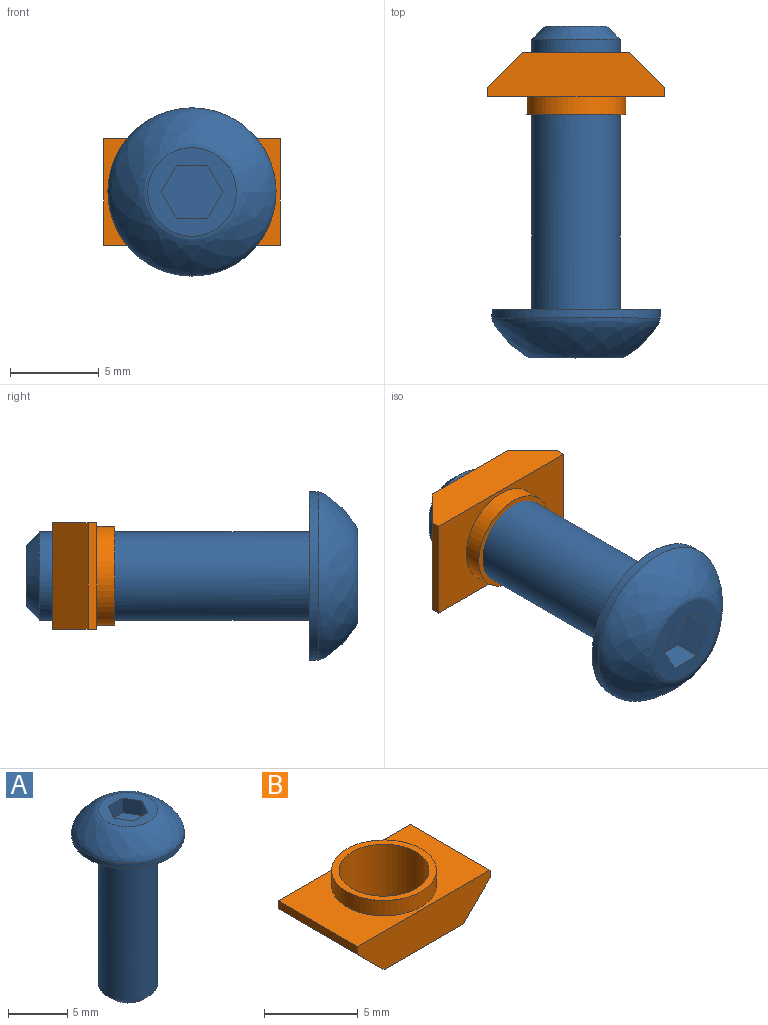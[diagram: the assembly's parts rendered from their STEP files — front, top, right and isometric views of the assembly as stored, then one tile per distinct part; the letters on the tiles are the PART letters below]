
ASSEMBLY  parts=2 mates=1
PART A: 14 faces, bbox 9.5x9.5x18.8 mm
  f0: plane 5.01x5.01mm, normal (0,0,1), area 11.8mm2, adj f3,f4,f5,f6,f7,f8,f10
  f1: cylinder r=4.75mm len=9.5mm, axis (0,0,-1), area 14.9mm2, adj f2,f10
  f2: plane 9.5x9.5mm, normal (0,0,-1), area 51.2mm2, adj f1,f11
  f3: plane 1.5x1.5mm, normal (-0.87,-0.5,0), area 2.6mm2, adj f0,f4,f8,f9
  f4: plane 1.73x1.5mm, normal (0,-1,0), area 2.6mm2, adj f0,f3,f5,f9
  f5: plane 1.5x1.5mm, normal (0.87,-0.5,0), area 2.6mm2, adj f0,f4,f6,f9
  f6: plane 1.5x1.5mm, normal (0.87,0.5,0), area 2.6mm2, adj f0,f5,f7,f9
  f7: plane 1.73x1.5mm, normal (0,1,0), area 2.6mm2, adj f0,f6,f8,f9
  f8: plane 1.5x1.5mm, normal (-0.87,0.5,0), area 2.6mm2, adj f0,f3,f7,f9
  f9: plane 3.46x3mm, normal (0,0,1), area 7.8mm2, adj f3,f4,f5,f6,f7,f8
  f10: bspline ~9.5x9.5mm, area 78.3mm2, adj f0,f1
  f11: cylinder r=2.5mm len=15.25mm, axis (0,0,1), area 239.5mm2, adj f2,f13
  f12: plane 3.5x3.5mm, normal (0,0,-1), area 9.6mm2, adj f13
  f13: cone r=1.75mm half-angle=45deg, axis (0,0,1), area 14.2mm2, adj f11,f12
PART B: 11 faces, bbox 10x6x3.5 mm
  f0: plane 10x2.5mm, normal (0,-1,0), area 21mm2, adj f1,f4,f5,f6,f9,f10
  f1: plane 6x0.5mm, normal (1,0,0), area 3mm2, adj f0,f2,f5,f10
  f2: plane 10x2.5mm, normal (0,1,0), area 21mm2, adj f1,f4,f5,f6,f9,f10
  f3: cylinder r=2.4mm len=4.8mm, axis (0,0,-1), area 52.8mm2, adj f6,f8
  f4: plane 6x0.5mm, normal (-1,0,0), area 3mm2, adj f0,f2,f5,f9
  f5: plane 10x6mm, normal (0,0,1), area 35.4mm2, adj f0,f1,f2,f4,f7
  f6: plane 6x6mm, normal (0,0,-1), area 17.9mm2, adj f0,f2,f3,f9,f10
  f7: cylinder r=2.8mm len=5.6mm, axis (0,0,-1), area 17.6mm2, adj f5,f8
  f8: plane 5.6x5.6mm, normal (0,0,1), area 6.5mm2, adj f3,f7
  f9: plane 6x2mm, normal (-0.71,0,-0.71), area 17mm2, adj f0,f2,f4,f6
  f10: plane 6x2mm, normal (0.71,0,-0.71), area 17mm2, adj f0,f1,f2,f6
PLACE A rot(axis=(1,0,0),90deg) t=(15,-11.5,-305)mm
PLACE B rot(axis=(1,0,0),90deg) t=(-10,3,-305)mm
MATE fastened A.f1 <-> B.f3  axis (0,1,0) through (-10,-11.5,-305)mm
